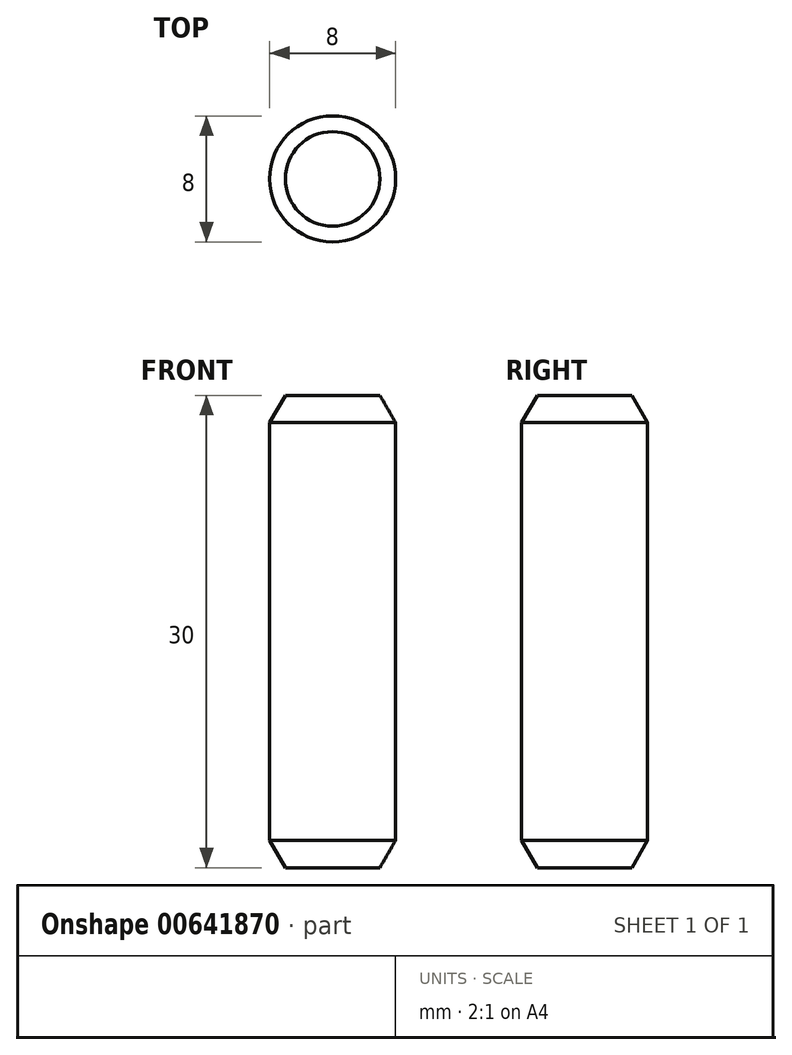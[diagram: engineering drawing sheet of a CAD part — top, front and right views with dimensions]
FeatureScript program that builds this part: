
annotation { "Feature Type Name" : "Feature", "Feature Type Description" : "" }
export const myFeature = defineFeature(function(context is Context, id is Id, definition is map)
    precondition{}
    {
        {
            var Q0;
            Q0=qCreatedBy(makeId("Front.planeOp"),FACE);
            var sketch = newSketch(context, id + "F0", { "sketchPlane" : qUnion([Q0])});
            skLineSegment(sketch, "E0.left", {"start": v(-4, 13.27) * mm, "end": v(-4, -13.27) * mm});
            skLineSegment(sketch, "E0.right", {"start": v(4, 13.27) * mm, "end": v(4, -13.27) * mm});
            skLineSegment(sketch, "E1", {"start": v(-4, 13.27) * mm, "end": v(-3, 15) * mm});
            skLineSegment(sketch, "E2", {"start": v(-3, 15) * mm, "end": v(3, 15) * mm});
            skLineSegment(sketch, "E3", {"start": v(3, 15) * mm, "end": v(4, 13.27) * mm});
            skLineSegment(sketch, "E4", {"start": v(-4, -13.27) * mm, "end": v(-3, -15) * mm});
            skLineSegment(sketch, "E5", {"start": v(-3, -15) * mm, "end": v(3, -15) * mm});
            skLineSegment(sketch, "E6", {"start": v(3, -15) * mm, "end": v(4, -13.27) * mm});
            skLineSegment(sketch, "E7", {"start": v(0, 15) * mm, "end": v(0, -15) * mm});
            skSolve(sketch);
        }
        {
            var Q0;
            Q0=makeQuery(id+"F0.imprint","IMPRINT",FACE,{"disambiguationData":[TD([[makeQuery(id+"F0.imprint","IMPRINT",EDGE,{"derivedFrom":sQuery(id+"F0.wireOp",EDGE,"E0.right")}),-1.0]])]});
            var Q1;
            Q1=sQuery(id+"F0.wireOp",EDGE,"E7");
            revolve(context, id + "F1", {"entities" : qUnion([Q0]), "axis" : qUnion([Q1]), "revolveType" : RevolveType.FULL});
        }
    });
